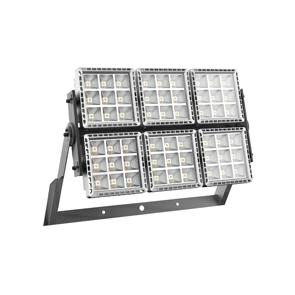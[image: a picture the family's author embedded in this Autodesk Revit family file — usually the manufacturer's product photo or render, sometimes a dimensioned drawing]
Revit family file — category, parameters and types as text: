
# Revit family: Lighting-Proiezione-GEWISS-SMART[PRO]2.0-PROIETTORI-LED-ALTA-POTENZA_6MODULI_CLI
name_source: partatom
category: Apparecchi per illuminazione
units: mm (PartAtom-declared; Revit-internal decimal feet)

## family parameters
Condiviso = No
Host = Superficie
Punto di calcolo locali = No
Quota connettore circolare = Usa diametro
Sorgente d'illuminazione = No
Taglio con vuoti quando caricato = No
Tipo di parte = Normale

## types (1)
- Lighting-Proiezione-GEWISS-SMART[PRO]2.0-PROIETTORI-LED-ALTA-POTENZA_6MODULI_CLI
    Alimentatore = Da ordinare separatamente
    Apparecchio a ridotta temperatura superficiale = No
    Applicazione = Interno / Esterno
    Cablaggio = Connettore stagno
    Caratteristiche elettriche e gestione della luce = -
    Caratteristiche ottiche e illuminotecniche = -
    Carico apparente = 1020 VA
    Catalogo = LIGHTING
    Certificazione DIN 18032-3 = -
    Certificazioni e classificazioni = -
    Classe fotobiologica = -
    Classe isolamento = I
    Classificazione = Lighting
    Classificazione: = -
    Codice digitale univoco (Datamatrix) = Attualmente non presente
    Colore = Grigio grafite
    Commenti Wattaggio 1_100 = Sì
    Commenti Wattaggio 1_200 = No
    Commenti sul wattaggio = 1020W
    Contesto = Illuminazione di grandi aree, impianti sportivi
    Controllo abbagliamento e luminanza = G*6 - ULOR = 0
    Corpo = Alluminio pressofuso
    Descrizione = SMART PRO 3x2M C4 CRI80 4000K
    Dispositivo di protezione = Secondo driver esterno
    Durata di vita = L90B10 (Tq+25°C) = 36000h L90B10 (Tq+50°C) = 26000h L80B10 (Tq+25°C) = 81000h
    Efficienza luminosa (lm/W) = 118
    Etichetta wattaggio = Sì
    Fine staffa = 484 mm  [stored 1.58793 ft]
    Finitura colore = Verniciato a polvere poliestere
    Fissaggio = Staffa
    Frequenza nominale (Hz) = -
    Gancio di chiusura = Viti metriche esagonali
    Garanzia = 5 anni
    Grado di protezione = IP66
    Gruppo ottico = Riflettore in PC HT quarzato&nbsp; e metallizzato lucido
    Guarnizioni = silicone antinvecchiamento
    H_centro_STaffa = 459 mm  [stored 1.50591 ft]
    IDF = ca142cd2-51eb-418c-bf0d-97266ef6bece
    IDT = 3f2d3c7146fd4f7e88ac85796f8f5998
    IPEA = STRADALE = A // GRANDI AREE = A3+ // CICLOPEDONALI = A+ // AREE VERDI = A+ // CENTRO STORICO = A4+ // ALTRO = A4+
    Immagine tipo = SMART PRO 6.jpg
    Inclinazione = Rotazione su staffa con goniometro integrato
    Indice di resa cromatica = CRI-80
    Informazioni generali = -
    Installazione e manutenzione = -
    L_plafoniera = 817 mm
    Lampada = LED
    Larghezza = 503 mm  [stored 1.65026 ft]
    Lumen output (lm) = 114500
    Materiali = -
    Modello = GWP2630AG840
    N. poli = 2
    Norma di riferimento = EN60598-1; EN60598-2-5; IEC 62778; IEC 62471; EN13201
    Ottica = C4 - Circolare 15°
    Ottica_ = GEWISS - OTTICA
    Peso (kg): = 29
    Potenza di sistema = 970W
    Produttore = GEWISS S.p.A.
    Prospetto di default = 1219 mm
    Resistenza agli urti = IK08
    Resistenza al filo incandescente = -
    SEO = Proiettore
    Scheda Tecnica = https://www.gewiss.com
    Schermo = Vetro piano extrachiaro spessore 4mm
    Sistema di controllo = Secondo driver esterno
    Sostituibilità gruppo ottico = Non disponibile
    Sostituibilità piastra di cablaggio = Si
    Spessore staffa = 59 mm  [stored 0.19357 ft]
    Struttura = GEWISS - NERO
    Struttura plafoniera = GEWISS - PLAFONIERA
    Superficie massima esposta al vento : = 0,333 m2
    Temperatura di colore = 4000K
    Temperatura di esercizio = -30 +50 °C
    Temperatura di stoccaggio = -
    Tensione di alimentazione = -
    Tipo di apparecchio = Apparecchio per proiezione LED di media e alta potenza
    Tipo di installazione e montaggio = Torrefaro - Parete - Terra
    Tipologia sorgente luminosa = LED - Non sostituibile
    Tolleranza cromatica = SDCM = 3
    Trasformatore = GEWISS - PLAFONIERA
    URL = https://www.gewiss.com
    Vano di alimentazione = Esterno
    Versione file RFA = 20.11
    Versioni = Luce naturale 4000K
    Vetro acceso = Lampada accesa
    Viti esterne = Acciaio inossidabile
    Voltaggio = 230 V

note: [stored X ft] marks values corroborated as IEEE doubles in the binary element streams (Revit-internal decimal feet)

## geometry (parser evidence)
native form markers: Blend x2
no freeform markers — native parametric forms only
